# Revit family: CAME_Створка_WING40
name_source: partatom
category: Специальное оборудование
units: mm (PartAtom-declared; Revit-internal decimal feet)

## family parameters
Всегда вертикально = Да
На основе рабочей плоскости = Нет
Общий = Да
При загрузке вырезать с полостями = Нет
Размер круглого соединителя = Использовать диаметр
Тип детали = Нормальный
Точка расчета площади = Нет

## types (4) — shared parameters
ADSK_URL документации изделия = https://camerussia.com
ADSK_URL страницы изделия = https://camerussia.com
ADSK_Версия Revit = 2019
ADSK_Версия семейства = 1.0
ADSK_Группирование = WING
ADSK_Единица измерения = шт.
ADSK_Завод-изготовитель = CAME
ADSK_Код изделия = Код КСР 26.30.50.119.61.2.07.09
ADSK_Количество = 1
ADSK_Обозначение = ТУ 26.30.50-001-89603926-2021
ADSK_Размер_Высота = 986 мм
ADSK_Размер_Диаметр = 174 мм
BL_BIM library = https://bimlib.pro
URL = https://camerussia.com
Группа модели = Турникеты
Изготовитель = CAME

## per-type parameters (varying)
| type | 600 | 900 | ADSK_Марка | ADSK_Масса | ADSK_Масса_Текст | ADSK_Наименование | ADSK_Наименование краткое | Материал створки | Описание |
| 600 оргстекло | Да | Нет | АРТ:001PSWL60 | 9 | 9 | Створка 600 мм из органического стекла для WING 40 | Створка 600 мм WING 40 из оргстекла | CAME_Стекло_Органическое | Створка Wing 600 мм из поликарбоната, с комплектом крепления створки. |
| 600 закаленное стекло | Да | Нет | АРТ:001PSWL60C | 15 | 15 | Створка 600 мм из закаленного стекла для WING 40 | Створка 600 мм WING 40 из зак. стекла | CAME_Стекло_Закаленное | Створка Wing 600 мм из 10 мм закаленного стекла, с комплектом крепления створки. |
| 900 закаленное стекло | Нет | Да | АРТ:001PSWL90C | 20 | 20 | Створка 900 мм из закаленного стекла для WING 40 | Створка 900 мм WING 40 из зак. стекла | CAME_Стекло_Закаленное | Створка Wing 900 мм из 10 мм закаленного стекла, с комплектом крепления створки. |
| 900 оргстекло | Нет | Да | АРТ:001PSWL90 | 12.15 | 12.15 | Створка 900 мм из органического стекла для WING 40 | Створка 900 мм WING 40 из оргстекла | CAME_Стекло_Органическое | Створка Wing 900 мм из 10 мм органического стекла, с комплектом крепления створки. |
